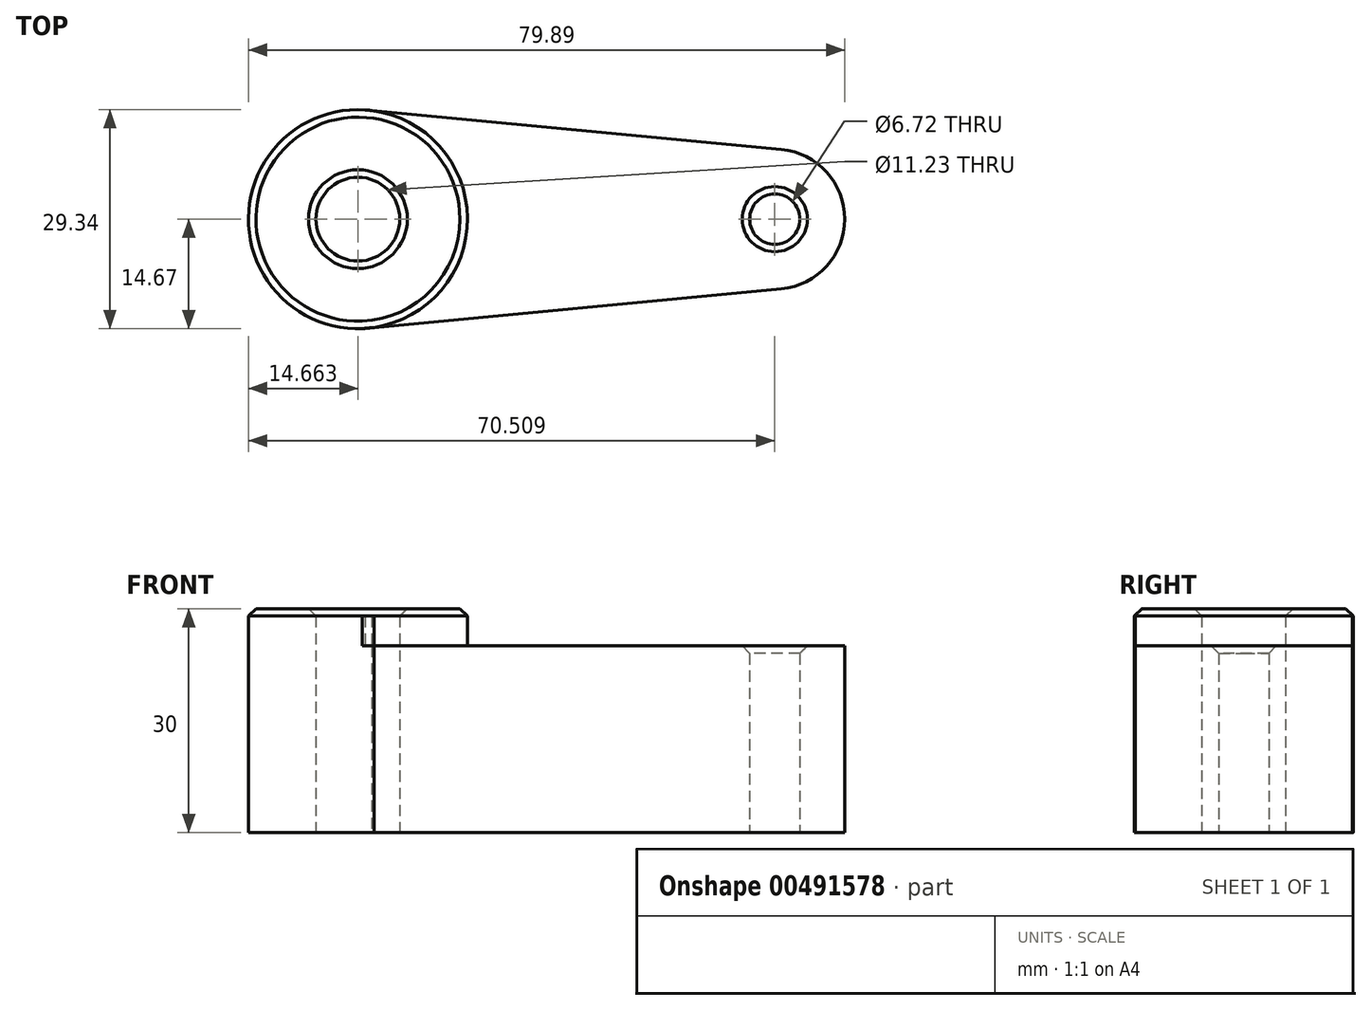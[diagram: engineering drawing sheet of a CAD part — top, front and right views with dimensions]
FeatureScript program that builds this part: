
annotation { "Feature Type Name" : "Feature", "Feature Type Description" : "" }
export const myFeature = defineFeature(function(context is Context, id is Id, definition is map)
    precondition{}
    {
        {
            var Q0;
            Q0=qCreatedBy(makeId("Top.planeOp"),FACE);
            var sketch = newSketch(context, id + "F0", { "sketchPlane" : qUnion([Q0])});
            skCircle(sketch, "E0", {"center": v(-34, 0) * mm, "radius": 14.67 * mm});
            skCircle(sketch, "E1", {"center": v(21.84, 0) * mm, "radius": 9.38 * mm});
            skLineSegment(sketch, "E2", {"start": v(-33.07, 14.64) * mm, "end": v(22.73, 9.34) * mm});
            skLineSegment(sketch, "E3", {"start": v(-33.4, -14.65) * mm, "end": v(22.72, -9.34) * mm});
            skCircle(sketch, "E4", {"center": v(-34, 0) * mm, "radius": 5.62 * mm});
            skCircle(sketch, "E5", {"center": v(21.84, 0) * mm, "radius": 3.36 * mm});
            skSolve(sketch);
        }
        {
            var Q0;
            Q0 = qSketchRegion(id + "F0", true);
            extrude(context, id + "F1", {"entities" : qUnion([Q0]), "depth" : 25 * mm});
        }
        {
            var Q0;
            Q0=makeQuery(id+"F0.imprint","IMPRINT",FACE,{"disambiguationData":[TD([[makeQuery(id+"F0.imprint","IMPRINT",EDGE,{"derivedFrom":sQuery(id+"F0.wireOp",EDGE,"E4")}),-1.0]])]});
            extrude(context, id + "F2", {"entities" : qUnion([Q0]), "operationType" : NewBodyOperationType.ADD, "depth" : 30 * mm});
        }
        {
            var Q0;
            Q0=makeQuery(id+"F2.opExtrude","CAP_EDGE",EDGE,{"disambiguationData":[OSD([sQuery(id+"F0.wireOp",EDGE,"E4")])],"isStart":false});
            var Q1;
            {var subQ0=sQuery(id+"F0.wireOp",EDGE,"E0");Q1=makeQuery(id+"F2.opExtrude","CAP_EDGE",EDGE,{"disambiguationData":[OSD([subQ0]),TDD([makeQuery(id+"F0.imprint","IMPRINT",EDGE,{"disambiguationData":[TD([[makeQuery(id+"F0.imprint","INTERSECT",VERTEX,{"disambiguationData":[OD(0.0)],"derivedFrom":[subQ0,sQuery(id+"F0.wireOp",EDGE,"E2")]}),-1.0]])],"derivedFrom":subQ0})])],"isStart":false});}
            var Q2;
            {var subQ0=sQuery(id+"F0.wireOp",EDGE,"E0");Q2=makeQuery(id+"F2.opExtrude","CAP_EDGE",EDGE,{"disambiguationData":[OSD([subQ0]),TDD([makeQuery(id+"F0.imprint","IMPRINT",EDGE,{"disambiguationData":[TD([[makeQuery(id+"F0.imprint","INTERSECT",VERTEX,{"disambiguationData":[OD(1.0)],"derivedFrom":[subQ0,sQuery(id+"F0.wireOp",EDGE,"E2")]}),1.0]])],"derivedFrom":subQ0})])],"isStart":false});}
            var Q3;
            Q3=makeQuery(id+"F1.opExtrude","CAP_EDGE",EDGE,{"disambiguationData":[OSD([sQuery(id+"F0.wireOp",EDGE,"E5")])],"isStart":false});
            chamfer(context, id + "F3", {"entities" : qUnion([Q0, Q1, Q2, Q3]), "width" : 1 * mm, "tangentPropagation" : true});
        }
    });
